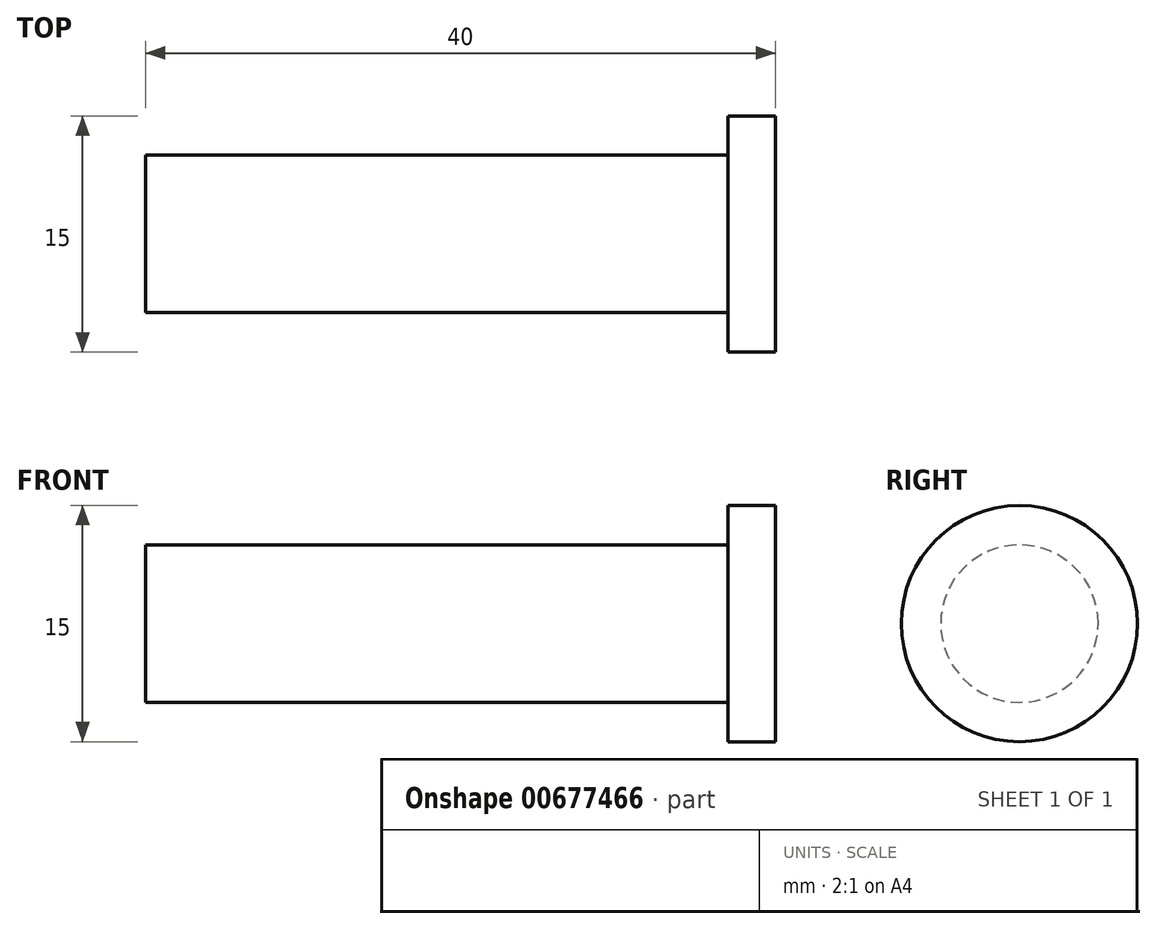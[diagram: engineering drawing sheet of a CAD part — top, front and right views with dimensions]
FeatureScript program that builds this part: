
annotation { "Feature Type Name" : "Feature", "Feature Type Description" : "" }
export const myFeature = defineFeature(function(context is Context, id is Id, definition is map)
    precondition{}
    {
        {
            var Q0;
            Q0=qCreatedBy(makeId("Front.planeOp"),FACE);
            var sketch = newSketch(context, id + "F0", { "sketchPlane" : qUnion([Q0])});
            skLineSegment(sketch, "E0", {"start": v(0, 0) * mm, "end": v(3, 0) * mm});
            skLineSegment(sketch, "E1", {"start": v(3, 0) * mm, "end": v(3, 7.5) * mm});
            skLineSegment(sketch, "E2", {"start": v(3, 7.5) * mm, "end": v(0, 7.5) * mm});
            skLineSegment(sketch, "E3", {"start": v(0, 7.5) * mm, "end": v(0, 5) * mm});
            skLineSegment(sketch, "E4", {"start": v(0, 5) * mm, "end": v(-37, 5) * mm});
            skLineSegment(sketch, "E5", {"start": v(-37, 5) * mm, "end": v(-37, 0) * mm});
            skLineSegment(sketch, "E6", {"start": v(-37, 0) * mm, "end": v(0, 0) * mm});
            skSolve(sketch);
        }
        {
            var Q0;
            Q0 = qSketchRegion(id + "F0", true);
            var Q1;
            Q1=sQuery(id+"F0.wireOp",EDGE,"E6");
            revolve(context, id + "F1", {"entities" : qUnion([Q0]), "axis" : qUnion([Q1]), "revolveType" : RevolveType.FULL});
        }
    });
